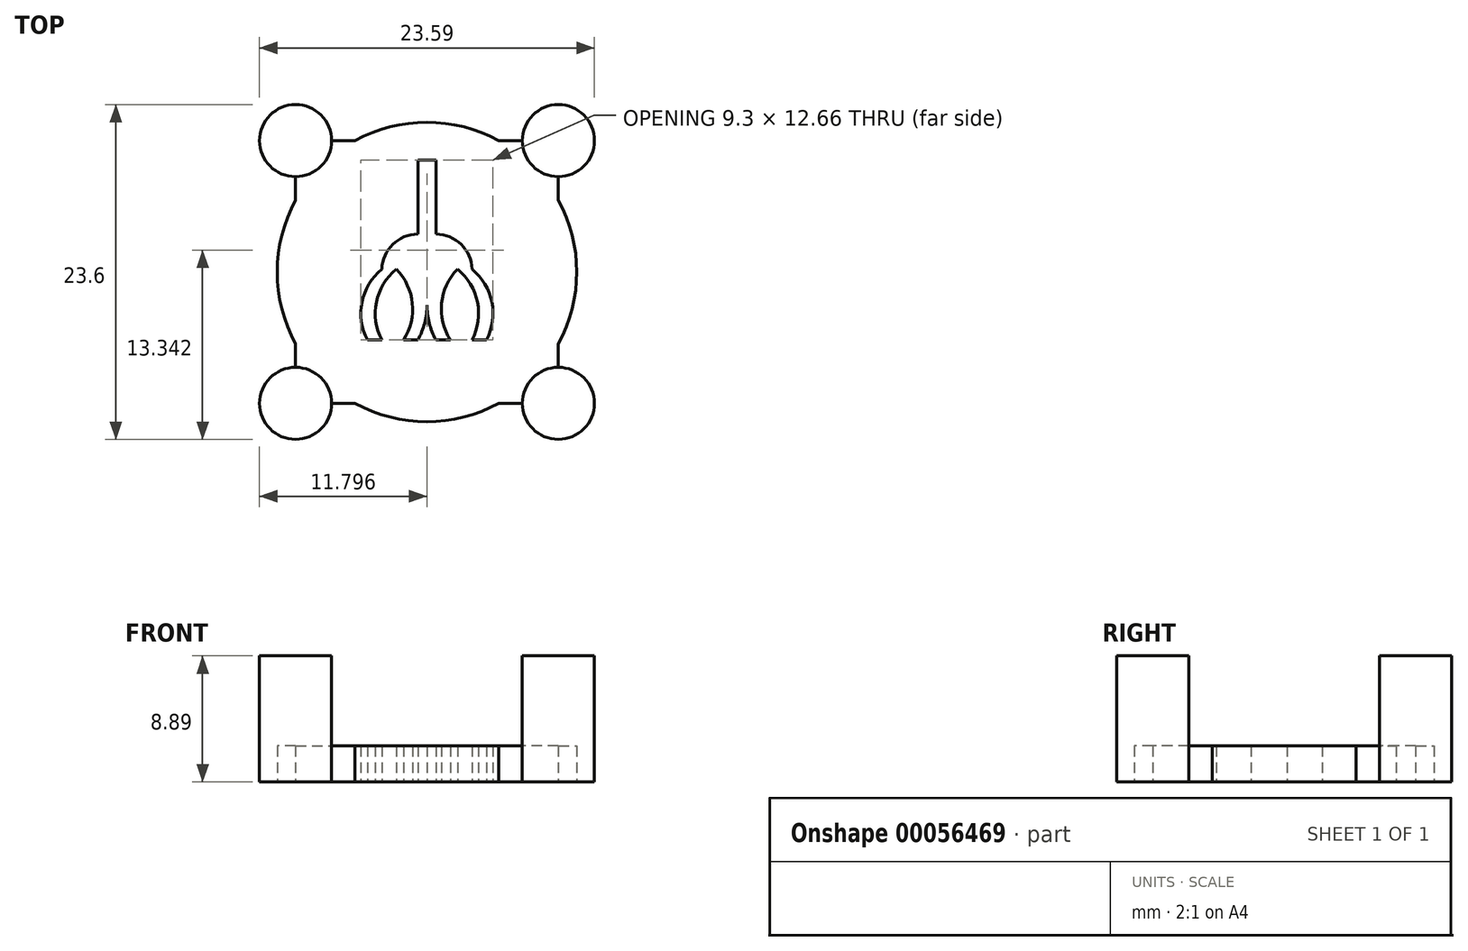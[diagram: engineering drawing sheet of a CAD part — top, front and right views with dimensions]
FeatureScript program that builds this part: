
annotation { "Feature Type Name" : "Feature", "Feature Type Description" : "" }
export const myFeature = defineFeature(function(context is Context, id is Id, definition is map)
    precondition{}
    {
        {
            var Q0;
            Q0=qCreatedBy(makeId("Top.planeOp"),FACE);
            var sketch = newSketch(context, id + "F0", { "sketchPlane" : qUnion([Q0])});
            skPoint(sketch, "E0", {"position": v(0, 14.05) * mm});
            skPoint(sketch, "E1", {"position": v(18.51, 14.05) * mm});
            skPoint(sketch, "E2", {"position": v(18.51, -4.47) * mm});
            skPoint(sketch, "E3", {"position": v(0, -4.47) * mm});
            skLineSegment(sketch, "E4.bottom", {"start": v(0, 14.05) * mm, "end": v(4.2, 14.05) * mm});
            skLineSegment(sketch, "E4.top", {"start": v(2.54, -4.47) * mm, "end": v(15.97, -4.47) * mm});
            skLineSegment(sketch, "E4.left", {"start": v(0, 11.5) * mm, "end": v(0, -1.93) * mm});
            skLineSegment(sketch, "E4.right", {"start": v(18.51, 14.05) * mm, "end": v(18.51, -1.93) * mm});
            skPoint(sketch, "E5", {"position": v(0, 16.59) * mm});
            skPoint(sketch, "E6", {"position": v(18.51, 16.59) * mm});
            skPoint(sketch, "E7", {"position": v(18.51, -7) * mm});
            skPoint(sketch, "E8", {"position": v(0, -7) * mm});
            skArc(sketch, "E9", {"start": v(1.8, 12.25) * mm, "mid": v(-0.97, 16.4) * mm, "end": v(0, 11.5) * mm});
            skArc(sketch, "E10", {"start": v(18.51, 11.5) * mm, "mid": v(20.3, 15.84) * mm, "end": v(15.97, 14.05) * mm});
            skCircle(sketch, "E11", {"center": v(18.51, -4.47) * mm, "radius": 2.54 * mm});
            skCircle(sketch, "E12", {"center": v(0, -4.47) * mm, "radius": 2.54 * mm});
            skArc(sketch, "E13", {"start": v(14.32, 14.05) * mm, "mid": v(9.26, 15.34) * mm, "end": v(4.2, 14.05) * mm});
            skPoint(sketch, "E13.centerSnap0", {"position": v(9.26, 14.05) * mm});
            skPoint(sketch, "E13.centerSnap1", {"position": v(0, 4.79) * mm});
            skLineSegment(sketch, "E14", {"start": v(0, 11.5) * mm, "end": v(0, 9.85) * mm});
            skLineSegment(sketch, "E15", {"start": v(0, 9.85) * mm, "end": v(0, 11.5) * mm});
            skLineSegment(sketch, "E16", {"start": v(2.54, 14.05) * mm, "end": v(4.2, 14.05) * mm});
            skLineSegment(sketch, "E17", {"start": v(4.2, 14.05) * mm, "end": v(2.54, 14.05) * mm});
            skLineSegment(sketch, "E18", {"start": v(15.97, 14.05) * mm, "end": v(14.32, 14.05) * mm});
            skLineSegment(sketch, "E19", {"start": v(14.32, 14.05) * mm, "end": v(15.97, 14.05) * mm});
            skLineSegment(sketch, "E20", {"start": v(18.51, 9.85) * mm, "end": v(18.51, 11.5) * mm});
            skLineSegment(sketch, "E21", {"start": v(18.51, 11.5) * mm, "end": v(18.54, 9.84) * mm});
            skLineSegment(sketch, "E22", {"start": v(18.51, -1.93) * mm, "end": v(18.51, -0.27) * mm});
            skLineSegment(sketch, "E23", {"start": v(18.51, -0.27) * mm, "end": v(18.51, -1.93) * mm});
            skLineSegment(sketch, "E24", {"start": v(15.97, -4.47) * mm, "end": v(14.32, -4.47) * mm});
            skLineSegment(sketch, "E25", {"start": v(14.32, -4.47) * mm, "end": v(15.97, -4.47) * mm});
            skLineSegment(sketch, "E26", {"start": v(2.54, -4.47) * mm, "end": v(4.2, -4.47) * mm});
            skLineSegment(sketch, "E27", {"start": v(4.2, -4.47) * mm, "end": v(2.54, -4.47) * mm});
            skLineSegment(sketch, "E28.trimOffspring", {"start": v(14.32, 14.05) * mm, "end": v(18.51, 14.05) * mm});
            skArc(sketch, "E29.trimOffspring", {"start": v(0, 9.85) * mm, "mid": v(1.8, -2.67) * mm, "end": v(14.32, -4.47) * mm});
            skArc(sketch, "E30.trimOffspring", {"start": v(16.72, -2.67) * mm, "mid": v(19.7, 3.3) * mm, "end": v(18.51, 9.85) * mm});
            skSolve(sketch);
        }
        {
            var Q0;
            Q0 = qSketchRegion(id + "F0", true);
            extrude(context, id + "F1", {"entities" : qUnion([Q0]), "depth" : 2.54 * mm});
        }
        {
            var Q0;
            Q0=makeQuery(id+"F1.opExtrude","CAP_FACE",FACE,{"disambiguationData":[OSD([sQuery(id+"F0.wireOp",EDGE,"E4.left"),sQuery(id+"F0.wireOp",EDGE,"E9"),sQuery(id+"F0.wireOp",EDGE,"E10"),sQuery(id+"F0.wireOp",EDGE,"E11"),sQuery(id+"F0.wireOp",EDGE,"E12"),sQuery(id+"F0.wireOp",EDGE,"E13"),sQuery(id+"F0.wireOp",EDGE,"E15"),sQuery(id+"F0.wireOp",EDGE,"E17"),sQuery(id+"F0.wireOp",EDGE,"E20"),sQuery(id+"F0.wireOp",EDGE,"E23"),sQuery(id+"F0.wireOp",EDGE,"E25"),sQuery(id+"F0.wireOp",EDGE,"E27"),sQuery(id+"F0.wireOp",EDGE,"E28.trimOffspring"),sQuery(id+"F0.wireOp",EDGE,"E29.trimOffspring"),sQuery(id+"F0.wireOp",EDGE,"E30.trimOffspring")])],"isStart":false});
            var sketch = newSketch(context, id + "F2", { "sketchPlane" : qUnion([Q0])});
            skPoint(sketch, "E31", {"position": v(18.51, 14.05) * mm});
            skPoint(sketch, "E32", {"position": v(0, 14.05) * mm});
            skPoint(sketch, "E33", {"position": v(0, -4.47) * mm});
            skPoint(sketch, "E34", {"position": v(18.51, -4.47) * mm});
            skPoint(sketch, "E35", {"position": v(0, 16.59) * mm});
            skPoint(sketch, "E36", {"position": v(18.51, 16.59) * mm});
            skPoint(sketch, "E37", {"position": v(18.51, -1.93) * mm});
            skPoint(sketch, "E38", {"position": v(0, -1.93) * mm});
            skCircle(sketch, "E39", {"center": v(0, 14.05) * mm, "radius": 2.54 * mm});
            skCircle(sketch, "E40", {"center": v(18.51, 14.05) * mm, "radius": 2.54 * mm});
            skCircle(sketch, "E41", {"center": v(18.51, -4.47) * mm, "radius": 2.54 * mm});
            skCircle(sketch, "E42", {"center": v(0, -4.47) * mm, "radius": 2.54 * mm});
            skSolve(sketch);
        }
        {
            var Q0;
            Q0 = qSketchRegion(id + "F2", true);
            extrude(context, id + "F3", {"entities" : qUnion([Q0]), "operationType" : NewBodyOperationType.ADD, "depth" : 6.35 * mm});
        }
        {
            var Q0;
            Q0=makeQuery(id+"F1.opExtrude","CAP_FACE",FACE,{"disambiguationData":[OSD([sQuery(id+"F0.wireOp",EDGE,"E4.left"),sQuery(id+"F0.wireOp",EDGE,"E9"),sQuery(id+"F0.wireOp",EDGE,"E10"),sQuery(id+"F0.wireOp",EDGE,"E11"),sQuery(id+"F0.wireOp",EDGE,"E12"),sQuery(id+"F0.wireOp",EDGE,"E13"),sQuery(id+"F0.wireOp",EDGE,"E15"),sQuery(id+"F0.wireOp",EDGE,"E17"),sQuery(id+"F0.wireOp",EDGE,"E20"),sQuery(id+"F0.wireOp",EDGE,"E23"),sQuery(id+"F0.wireOp",EDGE,"E25"),sQuery(id+"F0.wireOp",EDGE,"E27"),sQuery(id+"F0.wireOp",EDGE,"E28.trimOffspring"),sQuery(id+"F0.wireOp",EDGE,"E29.trimOffspring"),sQuery(id+"F0.wireOp",EDGE,"E30.trimOffspring")])],"isStart":true});
            var sketch = newSketch(context, id + "F4", { "sketchPlane" : qUnion([Q0])});
            skLineSegment(sketch, "E43.bottom", {"start": v(8.62, -12.66) * mm, "end": v(9.9, -12.66) * mm});
            skLineSegment(sketch, "E43.top", {"start": v(8.62, -7.46) * mm, "end": v(9.9, -7.46) * mm});
            skLineSegment(sketch, "E43.left", {"start": v(8.62, -12.66) * mm, "end": v(8.62, -7.46) * mm});
            skLineSegment(sketch, "E43.right", {"start": v(9.9, -12.66) * mm, "end": v(9.9, -7.46) * mm});
            skArc(sketch, "E44", {"start": v(9.9, -7.46) * mm, "mid": v(11.66, -6.74) * mm, "end": v(12.43, -4.98) * mm});
            skArc(sketch, "E45", {"start": v(6.08, -4.98) * mm, "mid": v(6.85, -6.74) * mm, "end": v(8.62, -7.46) * mm});
            skArc(sketch, "E46", {"start": v(8.62, -4.92) * mm, "mid": v(9.26, -5.44) * mm, "end": v(9.9, -4.92) * mm});
            skArc(sketch, "E47", {"start": v(12.43, -4.98) * mm, "mid": v(13.83, -2.67) * mm, "end": v(13.45, 0) * mm});
            skArc(sketch, "E48", {"start": v(5.06, 0) * mm, "mid": v(4.68, -2.67) * mm, "end": v(6.08, -4.98) * mm});
            skPoint(sketch, "E49", {"position": v(19.8, -4.79) * mm});
            skPoint(sketch, "E50", {"position": v(-1.3, -4.79) * mm});
            skPoint(sketch, "E51", {"position": v(9.26, 5.76) * mm});
            skPoint(sketch, "E52", {"position": v(6.08, 0) * mm});
            skPoint(sketch, "E53", {"position": v(12.43, 0) * mm});
            skPoint(sketch, "E54", {"position": v(7.1, -4.98) * mm});
            skArc(sketch, "E55", {"start": v(6.08, 0) * mm, "mid": v(5.7, -2.67) * mm, "end": v(7.1, -4.98) * mm});
            skArc(sketch, "E56", {"start": v(7.1, -4.98) * mm, "mid": v(8.23, -2.58) * mm, "end": v(7.6, 0) * mm});
            skArc(sketch, "E57", {"start": v(8.62, -4.92) * mm, "mid": v(9.26, -2.46) * mm, "end": v(8.62, 0) * mm});
            skArc(sketch, "E58", {"start": v(9.9, 0) * mm, "mid": v(9.26, -2.46) * mm, "end": v(9.9, -4.92) * mm});
            skPoint(sketch, "E59", {"position": v(11.41, -4.98) * mm});
            skArc(sketch, "E60", {"start": v(11.41, -4.98) * mm, "mid": v(12.81, -2.67) * mm, "end": v(12.43, 0) * mm});
            skArc(sketch, "E61", {"start": v(10.9, 0) * mm, "mid": v(10.28, -2.58) * mm, "end": v(11.41, -4.98) * mm});
            skPoint(sketch, "E62", {"position": v(9.26, -2.46) * mm});
            skPoint(sketch, "E63", {"position": v(8.24, -2.46) * mm});
            skPoint(sketch, "E64", {"position": v(10.27, -2.46) * mm});
            skPoint(sketch, "E65", {"position": v(12.81, -2.67) * mm});
            skPoint(sketch, "E66", {"position": v(13.83, -2.67) * mm});
            skPoint(sketch, "E67", {"position": v(5.7, -2.67) * mm});
            skPoint(sketch, "E68", {"position": v(4.68, -2.67) * mm});
            skLineSegment(sketch, "E69", {"start": v(5.06, 0) * mm, "end": v(6.08, 0) * mm});
            skLineSegment(sketch, "E70", {"start": v(7.6, 0) * mm, "end": v(8.62, 0) * mm});
            skLineSegment(sketch, "E71", {"start": v(10.9, 0) * mm, "end": v(9.9, 0) * mm});
            skLineSegment(sketch, "E72", {"start": v(12.43, 0) * mm, "end": v(13.45, 0) * mm});
            skSolve(sketch);
        }
        {
            var Q0;
            Q0=makeQuery(id+"F4.imprint","IMPRINT",FACE,{"disambiguationData":[TD([[makeQuery(id+"F4.imprint","IMPRINT",EDGE,{"derivedFrom":sQuery(id+"F4.wireOp",EDGE,"E43.bottom")}),1.0]])]});
            var Q1;
            Q1=makeQuery(id+"F4.imprint","IMPRINT",FACE,{"disambiguationData":[TD([[makeQuery(id+"F4.imprint","IMPRINT",EDGE,{"derivedFrom":sQuery(id+"F4.wireOp",EDGE,"E43.top")}),1.0]])]});
            var Q2;
            {var subQ0=sQuery(id+"F4.wireOp",EDGE,"E46");Q2=makeQuery(id+"F4.imprint","IMPRINT",FACE,{"disambiguationData":[TD([[makeQuery(id+"F4.imprint","IMPRINT",EDGE,{"derivedFrom":subQ0}),1.0]])]});}
            extrude(context, id + "F5", {"entities" : qUnion([Q0, Q1, Q2]), "operationType" : NewBodyOperationType.REMOVE, "oppositeDirection" : true, "depth" : 25.4 * mm});
        }
    });
